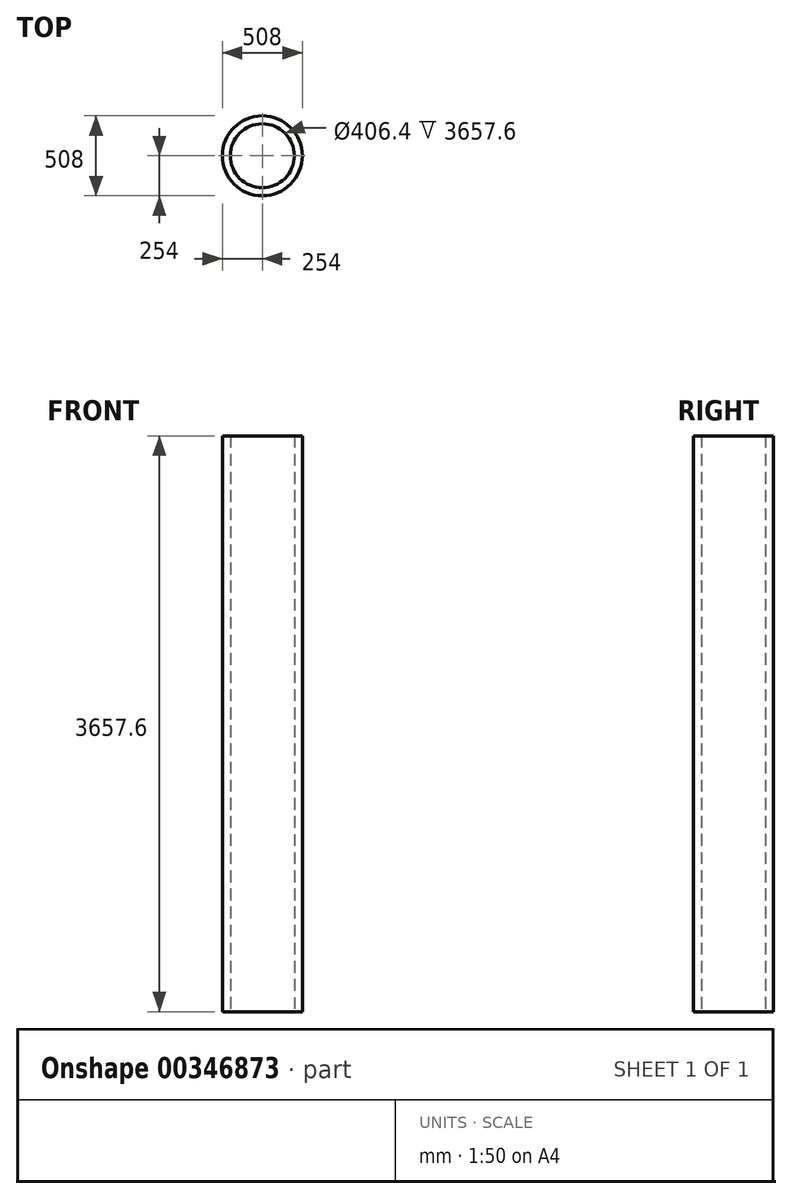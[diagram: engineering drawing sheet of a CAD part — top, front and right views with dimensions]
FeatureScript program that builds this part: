
annotation { "Feature Type Name" : "Feature", "Feature Type Description" : "" }
export const myFeature = defineFeature(function(context is Context, id is Id, definition is map)
    precondition{}
    {
        {
            var Q0;
            Q0=qCreatedBy(makeId("Top.planeOp"),FACE);
            var sketch = newSketch(context, id + "F0", { "sketchPlane" : qUnion([Q0])});
            skCircle(sketch, "E0", {"center": v(0, 0) * mm, "radius": 254 * mm});
            skCircle(sketch, "E1", {"center": v(0, 0) * mm, "radius": 203.2 * mm});
            skSolve(sketch);
        }
        {
            var Q0;
            Q0=makeQuery(id+"F0.imprint","IMPRINT",FACE,{"disambiguationData":[TD([[makeQuery(id+"F0.imprint","IMPRINT",EDGE,{"derivedFrom":sQuery(id+"F0.wireOp",EDGE,"E0")}),1.0]])]});
            extrude(context, id + "F1", {"entities" : qUnion([Q0]), "depth" : 3657.6 * mm});
        }
    });
